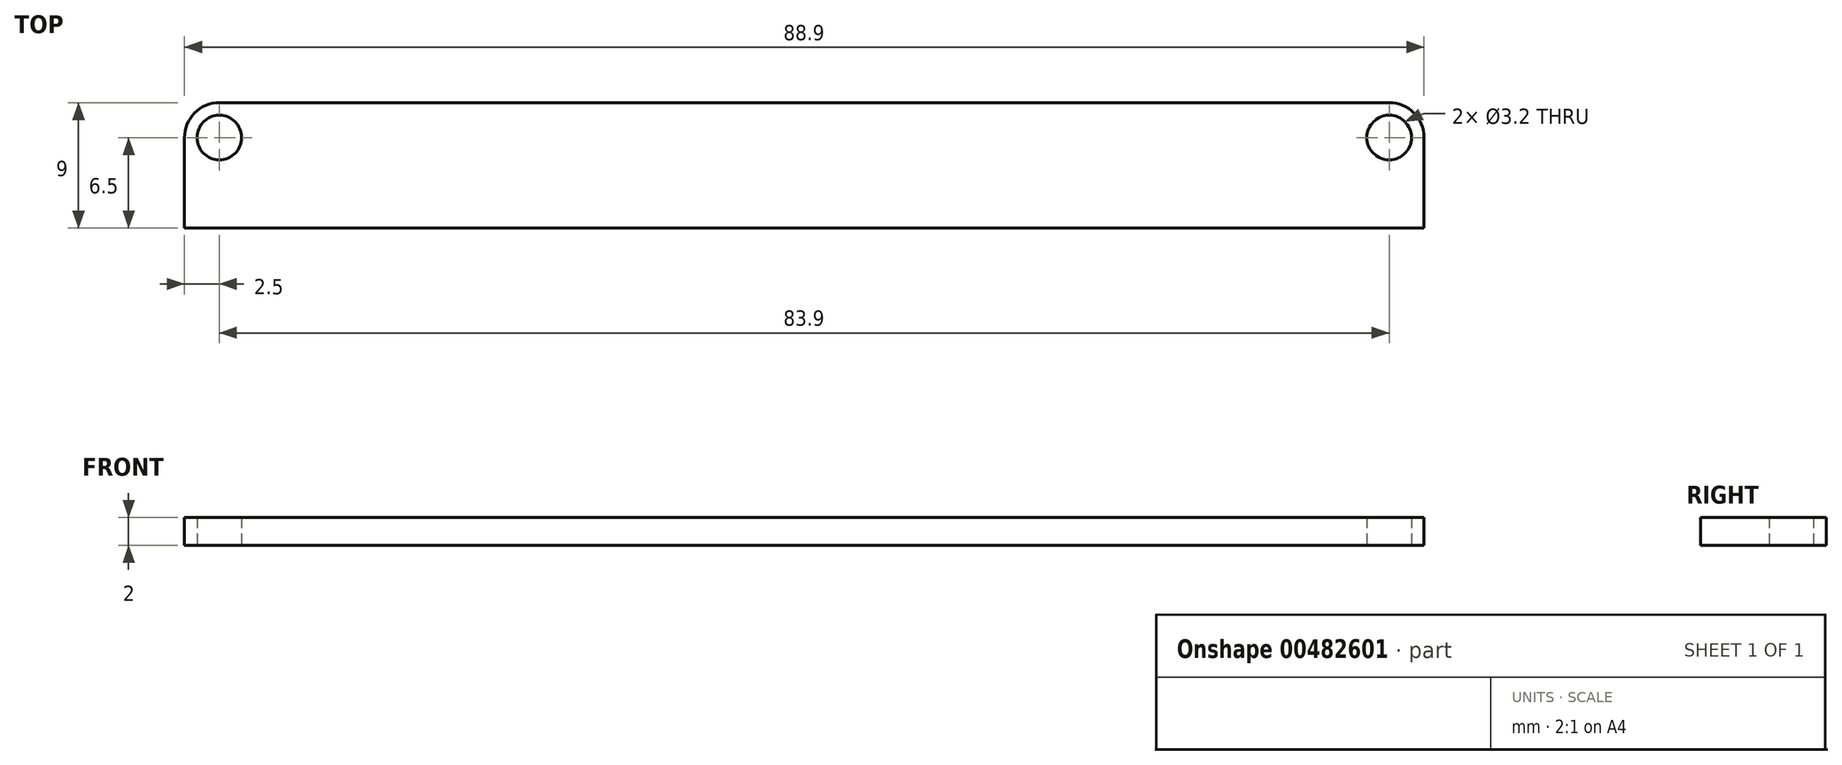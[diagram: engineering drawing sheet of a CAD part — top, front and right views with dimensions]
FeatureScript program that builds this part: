
annotation { "Feature Type Name" : "Feature", "Feature Type Description" : "" }
export const myFeature = defineFeature(function(context is Context, id is Id, definition is map)
    precondition{}
    {
        {
            var Q0;
            Q0=qCreatedBy(makeId("Top.planeOp"),FACE);
            var sketch = newSketch(context, id + "F0", { "sketchPlane" : qUnion([Q0])});
            skLineSegment(sketch, "E0.left", {"start": v(44.45, 23.5) * mm, "end": v(44.45, 27.5) * mm});
            skLineSegment(sketch, "E0.right", {"start": v(-44.45, 23.5) * mm, "end": v(-44.45, 27.5) * mm});
            skLineSegment(sketch, "E1.top", {"start": v(-41.95, 32.5) * mm, "end": v(41.95, 32.5) * mm});
            skLineSegment(sketch, "E1.left", {"start": v(-44.45, 27.5) * mm, "end": v(-44.45, 30) * mm});
            skLineSegment(sketch, "E1.right", {"start": v(44.45, 27.5) * mm, "end": v(44.45, 30) * mm});
            skPoint(sketch, "E2.visualSharp", {"position": v(-44.45, 32.5) * mm});
            skArc(sketch, "E2.filletArc", {"start": v(-41.95, 32.5) * mm, "mid": v(-43.72, 31.77) * mm, "end": v(-44.45, 30) * mm});
            skPoint(sketch, "E3.visualSharp", {"position": v(44.45, 32.5) * mm});
            skArc(sketch, "E3.filletArc", {"start": v(44.45, 30) * mm, "mid": v(43.72, 31.77) * mm, "end": v(41.95, 32.5) * mm});
            skCircle(sketch, "E4", {"center": v(-41.95, 30) * mm, "radius": 1.6 * mm});
            skLineSegment(sketch, "E5.trimOffspring", {"start": v(42.45, -32.45) * mm, "end": v(42.45, -32.5) * mm, "construction": true});
            skLineSegment(sketch, "E6", {"start": v(-44.45, 23.5) * mm, "end": v(44.45, 23.5) * mm});
            skCircle(sketch, "E7", {"center": v(41.95, 30) * mm, "radius": 1.6 * mm});
            skSolve(sketch);
        }
        {
            var Q0;
            Q0=makeQuery(id+"F0.imprint","IMPRINT",FACE,{"disambiguationData":[TD([[makeQuery(id+"F0.imprint","IMPRINT",EDGE,{"derivedFrom":sQuery(id+"F0.wireOp",EDGE,"E0.left")}),1.0]])]});
            extrude(context, id + "F1", {"entities" : qUnion([Q0]), "depth" : 2 * mm});
        }
    });
